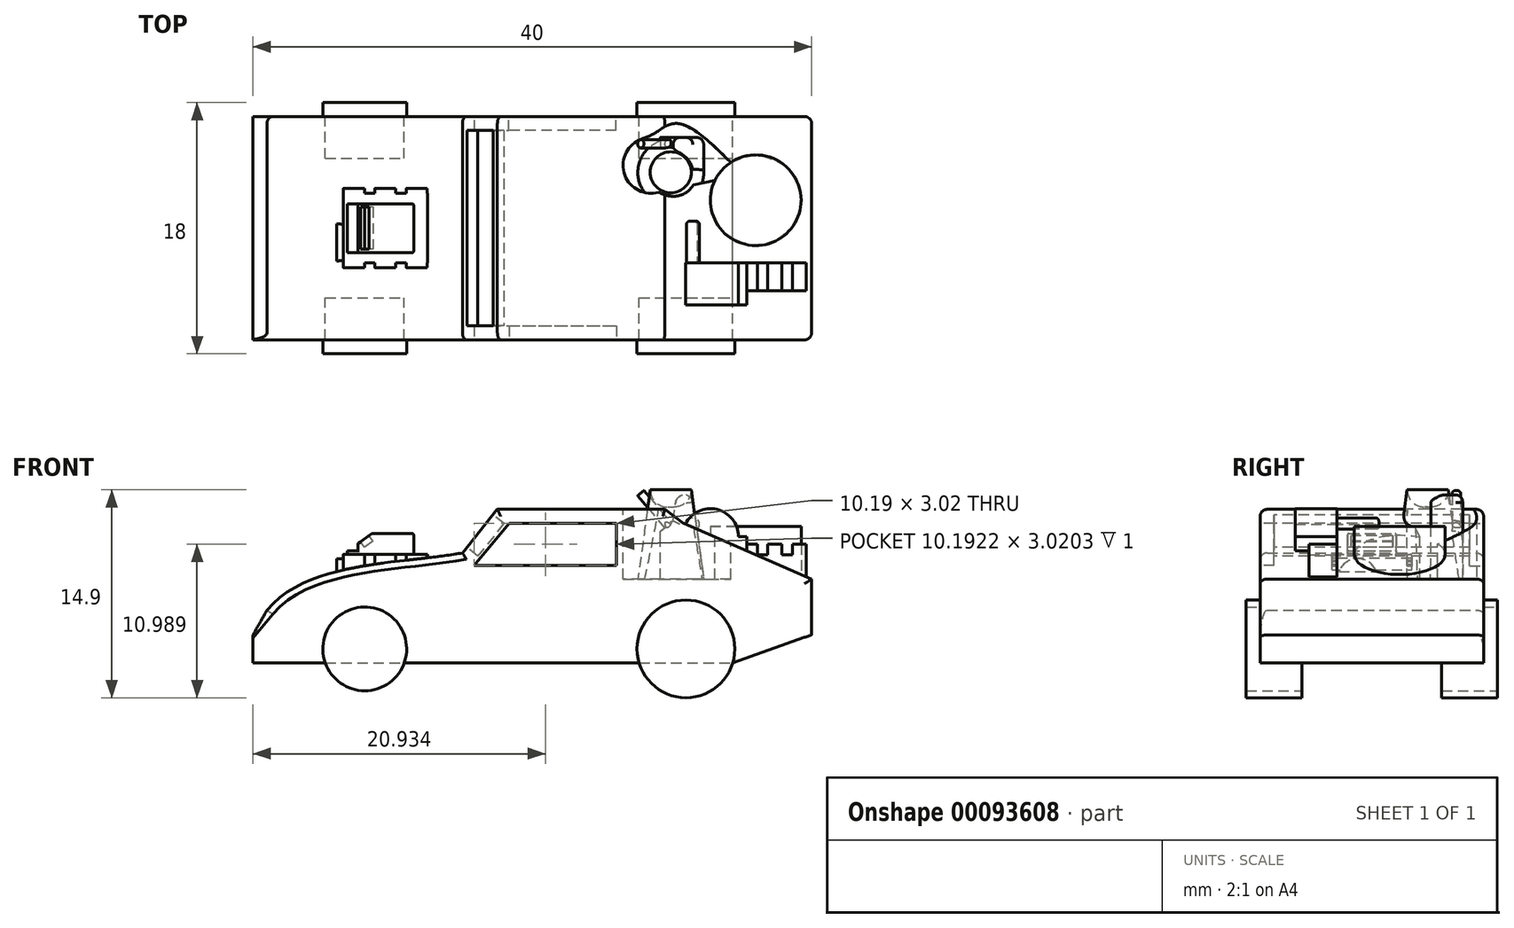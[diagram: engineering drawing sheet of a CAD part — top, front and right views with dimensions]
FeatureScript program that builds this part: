
annotation { "Feature Type Name" : "Feature", "Feature Type Description" : "" }
export const myFeature = defineFeature(function(context is Context, id is Id, definition is map)
    precondition{}
    {
        {
            var Q0;
            Q0=qCreatedBy(makeId("Front.planeOp"),FACE);
            var sketch = newSketch(context, id + "F0", { "sketchPlane" : qUnion([Q0])});
            skLineSegment(sketch, "E0", {"start": v(-19.08, 0) * mm, "end": v(19.92, 0) * mm});
            skLineSegment(sketch, "E1", {"start": v(19.92, 2.22) * mm, "end": v(19.92, -1.78) * mm});
            skLineSegment(sketch, "E2", {"start": v(19.92, -1.78) * mm, "end": v(14.24, -3.78) * mm});
            skLineSegment(sketch, "E3", {"start": v(19.92, 2.22) * mm, "end": v(10.77, 6.21) * mm});
            skLineSegment(sketch, "E4", {"start": v(10.74, 6.23) * mm, "end": v(9.42, 7.22) * mm});
            skLineSegment(sketch, "E5", {"start": v(9.42, 7.22) * mm, "end": v(-2.58, 7.22) * mm});
            skLineSegment(sketch, "E6", {"start": v(-2.58, 7.22) * mm, "end": v(-5.08, 4.1) * mm});
            skFitSpline(sketch, "E7", {"points": [v(-19.08, 0) * mm, v(-5.08, 4.1) * mm], "startDerivative": vector(8.6, 10.5) * mm, "endDerivative": vector(13.58, 2.41) * mm});
            skLineSegment(sketch, "E8", {"start": v(-19.08, 0) * mm, "end": v(-20.08, -1.78) * mm});
            skLineSegment(sketch, "E9", {"start": v(-20.08, -1.78) * mm, "end": v(-20.08, -3.78) * mm});
            skLineSegment(sketch, "E10", {"start": v(-20.08, -3.78) * mm, "end": v(14.24, -3.78) * mm});
            skPoint(sketch, "E11.visualSharp", {"position": v(10.75, 6.22) * mm});
            skArc(sketch, "E11.filletArc", {"start": v(10.74, 6.23) * mm, "mid": v(10.75, 6.22) * mm, "end": v(10.77, 6.21) * mm});
            skSolve(sketch);
        }
        {
            var Q0;
            Q0 = qSketchRegion(id + "F0", true);
            extrude(context, id + "F1", {"entities" : qUnion([Q0]), "endBound" : BoundingType.SYMMETRIC, "depth" : 16 * mm});
        }
        {
            var Q0;
            Q0=makeQuery(id+"F1.opExtrude","CAP_EDGE",EDGE,{"disambiguationData":[OSD([sQuery(id+"F0.wireOp",EDGE,"E7")])],"isStart":false});
            var Q1;
            Q1=makeQuery(id+"F1.opExtrude","CAP_EDGE",EDGE,{"disambiguationData":[OSD([sQuery(id+"F0.wireOp",EDGE,"E6")])],"isStart":false});
            var Q2;
            Q2=makeQuery(id+"F1.opExtrude","CAP_EDGE",EDGE,{"disambiguationData":[OSD([sQuery(id+"F0.wireOp",EDGE,"E5")])],"isStart":false});
            var Q3;
            Q3=makeQuery(id+"F1.opExtrude","CAP_EDGE",EDGE,{"disambiguationData":[OSD([sQuery(id+"F0.wireOp",EDGE,"E3")])],"isStart":false});
            var Q4;
            Q4=makeQuery(id+"F1.opExtrude","CAP_EDGE",EDGE,{"disambiguationData":[OSD([sQuery(id+"F0.wireOp",EDGE,"E4")])],"isStart":false});
            var Q5;
            Q5=makeQuery(id+"F1.opExtrude","CAP_EDGE",EDGE,{"disambiguationData":[OSD([sQuery(id+"F0.wireOp",EDGE,"E8")])],"isStart":true});
            var Q6;
            Q6=makeQuery(id+"F1.opExtrude","CAP_EDGE",EDGE,{"disambiguationData":[OSD([sQuery(id+"F0.wireOp",EDGE,"E7")])],"isStart":true});
            var Q7;
            Q7=makeQuery(id+"F1.opExtrude","CAP_EDGE",EDGE,{"disambiguationData":[OSD([sQuery(id+"F0.wireOp",EDGE,"E6")])],"isStart":true});
            var Q8;
            Q8=makeQuery(id+"F1.opExtrude","CAP_EDGE",EDGE,{"disambiguationData":[OSD([sQuery(id+"F0.wireOp",EDGE,"E5")])],"isStart":true});
            var Q9;
            Q9=makeQuery(id+"F1.opExtrude","CAP_EDGE",EDGE,{"disambiguationData":[OSD([sQuery(id+"F0.wireOp",EDGE,"E4")])],"isStart":true});
            var Q10;
            Q10=makeQuery(id+"F1.opExtrude","CAP_EDGE",EDGE,{"disambiguationData":[OSD([sQuery(id+"F0.wireOp",EDGE,"E3")])],"isStart":true});
            var Q11;
            Q11=makeQuery(id+"F1.opExtrude","CAP_EDGE",EDGE,{"disambiguationData":[OSD([sQuery(id+"F0.wireOp",EDGE,"E1")])],"isStart":false});
            var Q12;
            Q12=makeQuery(id+"F1.opExtrude","CAP_EDGE",EDGE,{"disambiguationData":[OSD([sQuery(id+"F0.wireOp",EDGE,"E1")])],"isStart":true});
            fillet(context, id + "F2", {"entities" : qUnion([Q0, Q1, Q2, Q3, Q4, Q5, Q6, Q7, Q8, Q9, Q10, Q11, Q12]), "radius" : 0.5 * mm, "tangentPropagation" : true, "allowEdgeOverflow" : false});
        }
        {
            var Q0;
            Q0=qCreatedBy(makeId("Top.planeOp"),FACE);
            var sketch = newSketch(context, id + "F3", { "sketchPlane" : qUnion([Q0])});
            skLineSegment(sketch, "E12.bottom", {"start": v(-13.58, 2.5) * mm, "end": v(-7.58, 2.5) * mm});
            skLineSegment(sketch, "E12.top", {"start": v(-13.58, -2.5) * mm, "end": v(-7.58, -2.5) * mm});
            skLineSegment(sketch, "E12.left", {"start": v(-13.58, 2.5) * mm, "end": v(-13.58, -2.5) * mm});
            skLineSegment(sketch, "E12.right", {"start": v(-7.58, 2.5) * mm, "end": v(-7.58, -2.5) * mm});
            skSolve(sketch);
        }
        {
            var Q0;
            Q0 = qSketchRegion(id + "F3", true);
            extrude(context, id + "F4", {"entities" : qUnion([Q0]), "operationType" : NewBodyOperationType.ADD, "depth" : 4 * mm});
        }
        {
            var Q0;
            Q0=qCreatedBy(makeId("Front.planeOp"),FACE);
            var sketch = newSketch(context, id + "F5", { "sketchPlane" : qUnion([Q0])});
            skLineSegment(sketch, "E13", {"start": v(-8.58, 4) * mm, "end": v(-12.58, 4) * mm});
            skLineSegment(sketch, "E14", {"start": v(-12.58, 4.25) * mm, "end": v(-12.58, 4.75) * mm});
            skLineSegment(sketch, "E15", {"start": v(-12.58, 4.75) * mm, "end": v(-11.58, 5.48) * mm});
            skLineSegment(sketch, "E16", {"start": v(-11.58, 5.48) * mm, "end": v(-8.58, 5.48) * mm});
            skLineSegment(sketch, "E17", {"start": v(-8.58, 5.48) * mm, "end": v(-8.58, 4) * mm});
            skLineSegment(sketch, "E18", {"start": v(-12.58, 4) * mm, "end": v(-13.33, 4) * mm});
            skLineSegment(sketch, "E19", {"start": v(-13.33, 4) * mm, "end": v(-13.33, 4.25) * mm});
            skLineSegment(sketch, "E20", {"start": v(-13.33, 4.25) * mm, "end": v(-12.58, 4.25) * mm});
            skSolve(sketch);
        }
        {
            var Q0;
            Q0 = qSketchRegion(id + "F5", true);
            extrude(context, id + "F6", {"entities" : qUnion([Q0]), "operationType" : NewBodyOperationType.ADD, "endBound" : BoundingType.SYMMETRIC, "depth" : 3.5 * mm});
        }
        {
            var Q0;
            Q0=makeQuery(id+"F6.opExtrude","SWEPT_FACE",FACE,{"disambiguationData":[OSD([sQuery(id+"F5.wireOp",EDGE,"E15")])]});
            var sketch = newSketch(context, id + "F7", { "sketchPlane" : qUnion([Q0])});
            skLineSegment(sketch, "E21.bottom", {"start": v(-6.36, 1.5) * mm, "end": v(-7.1, 1.5) * mm});
            skLineSegment(sketch, "E21.top", {"start": v(-6.36, -1.5) * mm, "end": v(-7.1, -1.5) * mm});
            skLineSegment(sketch, "E21.left", {"start": v(-6.36, 1.5) * mm, "end": v(-6.36, -1.5) * mm});
            skLineSegment(sketch, "E21.right", {"start": v(-7.1, 1.5) * mm, "end": v(-7.1, -1.5) * mm});
            skSolve(sketch);
        }
        {
            var Q0;
            Q0 = qSketchRegion(id + "F7", true);
            extrude(context, id + "F8", {"entities" : qUnion([Q0]), "operationType" : NewBodyOperationType.REMOVE, "oppositeDirection" : true, "depth" : 0.5 * mm});
        }
        {
            var Q0;
            Q0=makeQuery(id+"F4.opExtrude","SWEPT_FACE",FACE,{"disambiguationData":[OSD([sQuery(id+"F3.wireOp",EDGE,"E12.left")])]});
            var sketch = newSketch(context, id + "F9", { "sketchPlane" : qUnion([Q0])});
            skCircle(sketch, "E22", {"center": v(1.02, 2.25) * mm, "radius": 1.43 * mm});
            skSolve(sketch);
        }
        {
            var Q0;
            Q0 = qSketchRegion(id + "F9", true);
            extrude(context, id + "F10", {"entities" : qUnion([Q0]), "operationType" : NewBodyOperationType.ADD, "depth" : 0.5 * mm});
        }
        {
            var Q0;
            Q0=qCreatedBy(makeId("Front.planeOp"),FACE);
            var sketch = newSketch(context, id + "F11", { "sketchPlane" : qUnion([Q0])});
            skLineSegment(sketch, "E23", {"start": v(-13.6, 4) * mm, "end": v(-13.6, 2) * mm});
            skLineSegment(sketch, "E24", {"start": v(-13.6, 2) * mm, "end": v(-7.6, 2) * mm});
            skLineSegment(sketch, "E25", {"start": v(-7.6, 2) * mm, "end": v(-7.6, 4) * mm});
            skLineSegment(sketch, "E26", {"start": v(-7.6, 2.66) * mm, "end": v(-7.6, 4) * mm});
            skLineSegment(sketch, "E27", {"start": v(-7.6, 4) * mm, "end": v(-9.1, 4) * mm});
            skLineSegment(sketch, "E28", {"start": v(-9.1, 4) * mm, "end": v(-9.1, 2.66) * mm});
            skLineSegment(sketch, "E29", {"start": v(-9.1, 2.66) * mm, "end": v(-9.86, 2.66) * mm});
            skLineSegment(sketch, "E30", {"start": v(-9.86, 2.66) * mm, "end": v(-9.86, 4) * mm});
            skLineSegment(sketch, "E31", {"start": v(-9.86, 4) * mm, "end": v(-11.36, 4) * mm});
            skLineSegment(sketch, "E32", {"start": v(-11.36, 4) * mm, "end": v(-11.36, 2.45) * mm});
            skLineSegment(sketch, "E33", {"start": v(-11.36, 2.45) * mm, "end": v(-12.1, 2.45) * mm});
            skLineSegment(sketch, "E34", {"start": v(-12.1, 2.45) * mm, "end": v(-12.1, 4) * mm});
            skLineSegment(sketch, "E35", {"start": v(-12.1, 4) * mm, "end": v(-13.6, 4) * mm});
            skSolve(sketch);
        }
        {
            var Q0;
            Q0 = qSketchRegion(id + "F11", true);
            extrude(context, id + "F12", {"entities" : qUnion([Q0]), "operationType" : NewBodyOperationType.ADD, "endBound" : BoundingType.SYMMETRIC, "depth" : 5.7 * mm});
        }
        {
            var Q0;
            Q0=makeQuery(id+"F12.opExtrude","CAP_EDGE",EDGE,{"disambiguationData":[OSD([sQuery(id+"F11.wireOp",EDGE,"E35")])],"isStart":false});
            var Q1;
            Q1=makeQuery(id+"F12.opExtrude","CAP_EDGE",EDGE,{"disambiguationData":[OSD([sQuery(id+"F11.wireOp",EDGE,"E31")])],"isStart":false});
            var Q2;
            Q2=makeQuery(id+"F12.opExtrude","CAP_EDGE",EDGE,{"disambiguationData":[OSD([sQuery(id+"F11.wireOp",EDGE,"E27")])],"isStart":false});
            var Q3;
            Q3=makeQuery(id+"F12.opExtrude","CAP_EDGE",EDGE,{"disambiguationData":[OSD([sQuery(id+"F11.wireOp",EDGE,"E31")])],"isStart":true});
            var Q4;
            Q4=makeQuery(id+"F12.opExtrude","CAP_EDGE",EDGE,{"disambiguationData":[OSD([sQuery(id+"F11.wireOp",EDGE,"E35")])],"isStart":true});
            var Q5;
            Q5=makeQuery(id+"F12.opExtrude","CAP_EDGE",EDGE,{"disambiguationData":[OSD([sQuery(id+"F11.wireOp",EDGE,"E27")])],"isStart":true});
            var Q6;
            Q6=makeQuery(id+"F6.opExtrude","CAP_EDGE",EDGE,{"disambiguationData":[OSD([sQuery(id+"F5.wireOp",EDGE,"E15")])],"isStart":true});
            var Q7;
            Q7=makeQuery(id+"F6.opExtrude","CAP_EDGE",EDGE,{"disambiguationData":[OSD([sQuery(id+"F5.wireOp",EDGE,"E16")])],"isStart":true});
            var Q8;
            Q8=makeQuery(id+"F6.opExtrude","SWEPT_EDGE",EDGE,{"disambiguationData":[OSD([sQuery(id+"F5.wireOp",EDGE,"E16"),sQuery(id+"F5.wireOp",EDGE,"E17")])]});
            var Q9;
            Q9=makeQuery(id+"F6.opExtrude","CAP_EDGE",EDGE,{"disambiguationData":[OSD([sQuery(id+"F5.wireOp",EDGE,"E16")])],"isStart":false});
            var Q10;
            Q10=makeQuery(id+"F6.opExtrude","CAP_EDGE",EDGE,{"disambiguationData":[OSD([sQuery(id+"F5.wireOp",EDGE,"E15")])],"isStart":false});
            var Q11;
            Q11=makeQuery(id+"F6.opExtrude","SWEPT_EDGE",EDGE,{"disambiguationData":[OSD([sQuery(id+"F5.wireOp",EDGE,"E15"),sQuery(id+"F5.wireOp",EDGE,"E16")])]});
            var Q12;
            Q12=makeQuery(id+"F6.opExtrude","SWEPT_EDGE",EDGE,{"disambiguationData":[OSD([sQuery(id+"F5.wireOp",EDGE,"E14"),sQuery(id+"F5.wireOp",EDGE,"E15")])]});
            var Q13;
            Q13=makeQuery(id+"F6.opExtrude","CAP_EDGE",EDGE,{"disambiguationData":[OSD([sQuery(id+"F5.wireOp",EDGE,"E14")])],"isStart":false});
            var Q14;
            Q14=makeQuery(id+"F6.opExtrude","CAP_EDGE",EDGE,{"disambiguationData":[OSD([sQuery(id+"F5.wireOp",EDGE,"E14")])],"isStart":true});
            var Q15;
            Q15=makeQuery(id+"F6.opExtrude","CAP_EDGE",EDGE,{"disambiguationData":[OSD([sQuery(id+"F5.wireOp",EDGE,"E17")])],"isStart":false});
            var Q16;
            Q16=makeQuery(id+"F6.opExtrude","CAP_EDGE",EDGE,{"disambiguationData":[OSD([sQuery(id+"F5.wireOp",EDGE,"E17")])],"isStart":true});
            fillet(context, id + "F13", {"entities" : qUnion([Q0, Q1, Q2, Q3, Q4, Q5, Q6, Q7, Q8, Q9, Q10, Q11, Q12, Q13, Q14, Q15, Q16]), "radius" : 0.1 * mm, "tangentPropagation" : true, "allowEdgeOverflow" : false});
        }
        {
            var Q0;
            Q0=qCreatedBy(makeId("Front.planeOp"),FACE);
            cPlane(context, id + "F14", {"entities" : qUnion([Q0]), "cplaneType" : CPlaneType.OFFSET, "offset" : 2.5 * mm, "width" : 150 * mm, "height" : 150 * mm});
        }
        {
            var Q0;
            Q0=qCreatedBy(id+"F14.planeOp",FACE);
            var sketch = newSketch(context, id + "F15", { "sketchPlane" : qUnion([Q0])});
            skArc(sketch, "E36", {"start": v(14.68, 5.27) * mm, "mid": v(11.82, 7.08) * mm, "end": v(11.42, 3.72) * mm});
            skLineSegment(sketch, "E37", {"start": v(12.68, 5.27) * mm, "end": v(15.28, 5.27) * mm});
            skLineSegment(sketch, "E38", {"start": v(15.28, 5.27) * mm, "end": v(15.28, 3.72) * mm});
            skLineSegment(sketch, "E39", {"start": v(15.28, 3.72) * mm, "end": v(11.42, 3.72) * mm});
            skSolve(sketch);
        }
        {
            var Q0;
            Q0 = qSketchRegion(id + "F15", true);
            extrude(context, id + "F16", {"entities" : qUnion([Q0]), "operationType" : NewBodyOperationType.ADD, "depth" : 3 * mm});
        }
        {
            var Q0;
            Q0=qCreatedBy(id+"F14.planeOp",FACE);
            var sketch = newSketch(context, id + "F17", { "sketchPlane" : qUnion([Q0])});
            skLineSegment(sketch, "E40", {"start": v(14.73, 4.72) * mm, "end": v(16.03, 4.72) * mm});
            skLineSegment(sketch, "E41", {"start": v(16.03, 4.72) * mm, "end": v(16.03, 3.96) * mm});
            skLineSegment(sketch, "E42", {"start": v(16.78, 3.96) * mm, "end": v(16.78, 4.72) * mm});
            skLineSegment(sketch, "E43", {"start": v(16.78, 4.72) * mm, "end": v(17.78, 4.72) * mm});
            skLineSegment(sketch, "E44", {"start": v(17.78, 4.72) * mm, "end": v(17.78, 3.96) * mm});
            skLineSegment(sketch, "E45", {"start": v(18.53, 3.96) * mm, "end": v(18.53, 4.72) * mm});
            skLineSegment(sketch, "E46", {"start": v(16.03, 3.96) * mm, "end": v(16.78, 3.96) * mm});
            skLineSegment(sketch, "E47", {"start": v(17.78, 3.96) * mm, "end": v(18.53, 3.96) * mm});
            skLineSegment(sketch, "E48", {"start": v(18.53, 4.72) * mm, "end": v(19.53, 4.72) * mm});
            skLineSegment(sketch, "E49", {"start": v(19.53, 4.72) * mm, "end": v(19.53, 1.8) * mm});
            skLineSegment(sketch, "E50", {"start": v(19.53, 1.8) * mm, "end": v(14.73, 1.8) * mm});
            skLineSegment(sketch, "E51", {"start": v(14.73, 1.8) * mm, "end": v(14.73, 4.72) * mm});
            skPoint(sketch, "E52.orphan", {"position": v(15.29, 4.72) * mm});
            skPoint(sketch, "E53.start.orphan", {"position": v(16.03, 3.2) * mm});
            skPoint(sketch, "E54.orphan", {"position": v(16.78, 3.2) * mm});
            skSolve(sketch);
        }
        {
            var Q0;
            Q0 = qSketchRegion(id + "F17", true);
            extrude(context, id + "F18", {"entities" : qUnion([Q0]), "operationType" : NewBodyOperationType.ADD, "depth" : 2 * mm});
        }
        {
            var Q0;
            Q0=qCreatedBy(makeId("Top.planeOp"),FACE);
            var sketch = newSketch(context, id + "F19", { "sketchPlane" : qUnion([Q0])});
            skCircle(sketch, "E55", {"center": v(15.92, 2) * mm, "radius": 3.25 * mm});
            skSolve(sketch);
        }
        {
            var Q0;
            Q0 = qSketchRegion(id + "F19", true);
            extrude(context, id + "F20", {"entities" : qUnion([Q0]), "operationType" : NewBodyOperationType.ADD, "depth" : 6 * mm});
        }
        {
            var Q0;
            Q0=makeQuery(id+"F18.boolean.opBoolean","MERGE",FACE,{"derivedFrom":[makeQuery(id+"F16.opExtrude","CAP_FACE",FACE,{"disambiguationData":[OSD([sQuery(id+"F15.wireOp",EDGE,"E36"),sQuery(id+"F15.wireOp",EDGE,"E37"),sQuery(id+"F15.wireOp",EDGE,"E38"),sQuery(id+"F15.wireOp",EDGE,"E39")])],"isStart":true}),makeQuery(id+"F18.opExtrude","CAP_FACE",FACE,{"disambiguationData":[OSD([sQuery(id+"F17.wireOp",EDGE,"E40"),sQuery(id+"F17.wireOp",EDGE,"E41"),sQuery(id+"F17.wireOp",EDGE,"E42"),sQuery(id+"F17.wireOp",EDGE,"E43"),sQuery(id+"F17.wireOp",EDGE,"E44"),sQuery(id+"F17.wireOp",EDGE,"E45"),sQuery(id+"F17.wireOp",EDGE,"E46"),sQuery(id+"F17.wireOp",EDGE,"E47"),sQuery(id+"F17.wireOp",EDGE,"E48"),sQuery(id+"F17.wireOp",EDGE,"E49"),sQuery(id+"F17.wireOp",EDGE,"E50"),sQuery(id+"F17.wireOp",EDGE,"E51")])],"isStart":true})]});
            var sketch = newSketch(context, id + "F21", { "sketchPlane" : qUnion([Q0])});
            skCircle(sketch, "E56", {"center": v(-11.42, 6.15) * mm, "radius": 0.47 * mm});
            skSolve(sketch);
        }
        {
            var Q0;
            Q0 = qSketchRegion(id + "F21", true);
            extrude(context, id + "F22", {"entities" : qUnion([Q0]), "operationType" : NewBodyOperationType.ADD, "depth" : 3 * mm});
        }
        {
            var Q0;
            Q0=makeQuery(id+"F22.opExtrude","CAP_EDGE",EDGE,{"disambiguationData":[OSD([sQuery(id+"F21.wireOp",EDGE,"E56")])],"isStart":false});
            fillet(context, id + "F23", {"entities" : qUnion([Q0]), "radius" : 0.25 * mm, "tangentPropagation" : true, "allowEdgeOverflow" : false});
        }
        {
            var Q0;
            Q0=makeQuery(id+"F1.opExtrude","SWEPT_FACE",FACE,{"disambiguationData":[OSD([sQuery(id+"F0.wireOp",EDGE,"E5")])]});
            var sketch = newSketch(context, id + "F24", { "sketchPlane" : qUnion([Q0])});
            skArc(sketch, "E57", {"start": v(7.77, 6.4) * mm, "mid": v(6.55, 3.78) * mm, "end": v(9.21, 2.67) * mm});
            skFitSpline(sketch, "E58", {"points": [v(8.39, 6.5) * mm, v(10.32, 7.5) * mm, v(14.03, 4.82) * mm], "startDerivative": vector(4.42, 3.87) * mm, "endDerivative": vector(6.71, -6.6) * mm});
            skLineSegment(sketch, "E59", {"start": v(9.21, 2.67) * mm, "end": v(13, 3.43) * mm});
            skArc(sketch, "E60", {"start": v(14.13, 4.72) * mm, "mid": v(13.48, 4.15) * mm, "end": v(13, 3.43) * mm});
            skLineSegment(sketch, "E61", {"start": v(14.03, 4.82) * mm, "end": v(14.13, 4.72) * mm});
            skArc(sketch, "E62.filletArc", {"start": v(7.77, 6.4) * mm, "mid": v(8.45, 6.68) * mm, "end": v(9.08, 7.06) * mm});
            skSolve(sketch);
        }
        {
            var Q0;
            Q0 = qSketchRegion(id + "F24", true);
            extrude(context, id + "F25", {"entities" : qUnion([Q0]), "operationType" : NewBodyOperationType.REMOVE, "oppositeDirection" : true, "depth" : 5 * mm});
        }
        {
            var Q0;
            Q0=makeQuery(id+"F1.opExtrude","CAP_FACE",FACE,{"disambiguationData":[OSD([sQuery(id+"F0.wireOp",EDGE,"E1"),sQuery(id+"F0.wireOp",EDGE,"E2"),sQuery(id+"F0.wireOp",EDGE,"E3"),sQuery(id+"F0.wireOp",EDGE,"E4"),sQuery(id+"F0.wireOp",EDGE,"E5"),sQuery(id+"F0.wireOp",EDGE,"E6"),sQuery(id+"F0.wireOp",EDGE,"E7"),sQuery(id+"F0.wireOp",EDGE,"E8"),sQuery(id+"F0.wireOp",EDGE,"E9"),sQuery(id+"F0.wireOp",EDGE,"E10"),sQuery(id+"F0.wireOp",EDGE,"E11.filletArc")])],"isStart":true});
            cPlane(context, id + "F26", {"entities" : qUnion([Q0]), "cplaneType" : CPlaneType.OFFSET, "offset" : 4 * mm, "oppositeDirection" : true, "width" : 150 * mm, "height" : 150 * mm});
        }
        {
            var Q0;
            Q0=qCreatedBy(id+"F26.planeOp",FACE);
            var sketch = newSketch(context, id + "F27", { "sketchPlane" : qUnion([Q0])});
            skLineSegment(sketch, "E63", {"start": v(-9.84, 1.22) * mm, "end": v(-9.84, 9.86) * mm});
            skArc(sketch, "E64", {"start": v(-8.36, 8.62) * mm, "mid": v(-8.8, 9.58) * mm, "end": v(-9.84, 9.86) * mm});
            skLineSegment(sketch, "E65", {"start": v(-8.36, 8.62) * mm, "end": v(-7.34, 1.22) * mm});
            skLineSegment(sketch, "E66", {"start": v(-7.34, 1.22) * mm, "end": v(-9.84, 1.22) * mm});
            skLineSegment(sketch, "E67", {"start": v(-9.84, 9.86) * mm, "end": v(-9.84, 11.33) * mm});
            skSolve(sketch);
        }
        {
            var Q0;
            Q0 = qSketchRegion(id + "F27", true);
            var Q1;
            Q1=sQuery(id+"F27.wireOp",EDGE,"E67");
            revolve(context, id + "F28", {"operationType" : NewBodyOperationType.ADD, "entities" : qUnion([Q0]), "axis" : qUnion([Q1]), "revolveType" : RevolveType.FULL});
        }
        {
            var Q0;
            Q0=qCreatedBy(id+"F26.planeOp",FACE);
            var sketch = newSketch(context, id + "F29", { "sketchPlane" : qUnion([Q0])});
            skLineSegment(sketch, "E68", {"start": v(-11.41, 7.72) * mm, "end": v(-12.48, 0.2) * mm});
            skLineSegment(sketch, "E69", {"start": v(-12.48, 0.2) * mm, "end": v(-9.09, 0.2) * mm});
            skLineSegment(sketch, "E70", {"start": v(-9.09, 0.2) * mm, "end": v(-9.09, 5.64) * mm});
            skLineSegment(sketch, "E71", {"start": v(-9.09, 5.64) * mm, "end": v(-10, 6.41) * mm});
            skLineSegment(sketch, "E72", {"start": v(-10, 6.41) * mm, "end": v(-10.19, 7.72) * mm});
            skArc(sketch, "E73", {"start": v(-10.19, 7.72) * mm, "mid": v(-10.8, 8.25) * mm, "end": v(-11.41, 7.72) * mm});
            skPoint(sketch, "E74.orphan", {"position": v(-9.09, 7.72) * mm});
            skSolve(sketch);
        }
        {
            var Q0;
            Q0 = qSketchRegion(id + "F29", true);
            extrude(context, id + "F30", {"entities" : qUnion([Q0]), "operationType" : NewBodyOperationType.ADD, "depth" : 2.5 * mm});
        }
        {
            var Q0;
            Q0=makeQuery(id+"F30.opExtrude","SWEPT_FACE",FACE,{"disambiguationData":[OSD([sQuery(id+"F29.wireOp",EDGE,"E71")])]});
            var sketch = newSketch(context, id + "F31", { "sketchPlane" : qUnion([Q0])});
            skCircle(sketch, "E75", {"center": v(11.28, 6.05) * mm, "radius": 0.3 * mm});
            skSolve(sketch);
        }
        {
            var Q0;
            Q0 = qSketchRegion(id + "F31", true);
            extrude(context, id + "F32", {"entities" : qUnion([Q0]), "operationType" : NewBodyOperationType.ADD, "depth" : 3 * mm});
        }
        {
            var Q0;
            Q0=makeQuery(id+"F30.opExtrude","CAP_EDGE",EDGE,{"disambiguationData":[OSD([sQuery(id+"F29.wireOp",EDGE,"E68")])],"isStart":false});
            var Q1;
            Q1=makeQuery(id+"F30.opExtrude","CAP_EDGE",EDGE,{"disambiguationData":[OSD([sQuery(id+"F29.wireOp",EDGE,"E73")])],"isStart":false});
            var Q2;
            Q2=makeQuery(id+"F30.opExtrude","CAP_EDGE",EDGE,{"disambiguationData":[OSD([sQuery(id+"F29.wireOp",EDGE,"E72")])],"isStart":false});
            var Q3;
            Q3=makeQuery(id+"F30.opExtrude","CAP_EDGE",EDGE,{"disambiguationData":[OSD([sQuery(id+"F29.wireOp",EDGE,"E71")])],"isStart":false});
            fillet(context, id + "F33", {"entities" : qUnion([Q0, Q1, Q2, Q3]), "radius" : 0.5 * mm, "tangentPropagation" : true, "allowEdgeOverflow" : false});
        }
        {
            var Q0;
            Q0=makeQuery(id+"F1.opExtrude","SWEPT_FACE",FACE,{"disambiguationData":[OSD([sQuery(id+"F0.wireOp",EDGE,"E6")])]});
            var sketch = newSketch(context, id + "F34", { "sketchPlane" : qUnion([Q0])});
            skLineSegment(sketch, "E76.bottom", {"start": v(-7, 3.52) * mm, "end": v(7, 3.52) * mm});
            skLineSegment(sketch, "E76.top", {"start": v(-7, 0.52) * mm, "end": v(7, 0.52) * mm});
            skLineSegment(sketch, "E76.left", {"start": v(-7, 3.52) * mm, "end": v(-7, 0.52) * mm});
            skLineSegment(sketch, "E76.right", {"start": v(7, 3.52) * mm, "end": v(7, 0.52) * mm});
            skSolve(sketch);
        }
        {
            var Q0;
            Q0 = qSketchRegion(id + "F34", true);
            extrude(context, id + "F35", {"entities" : qUnion([Q0]), "operationType" : NewBodyOperationType.REMOVE, "oppositeDirection" : true, "depth" : 1 * mm});
        }
        {
            var Q0;
            Q0=makeQuery(id+"F1.opExtrude","CAP_FACE",FACE,{"disambiguationData":[OSD([sQuery(id+"F0.wireOp",EDGE,"E1"),sQuery(id+"F0.wireOp",EDGE,"E2"),sQuery(id+"F0.wireOp",EDGE,"E3"),sQuery(id+"F0.wireOp",EDGE,"E4"),sQuery(id+"F0.wireOp",EDGE,"E5"),sQuery(id+"F0.wireOp",EDGE,"E6"),sQuery(id+"F0.wireOp",EDGE,"E7"),sQuery(id+"F0.wireOp",EDGE,"E8"),sQuery(id+"F0.wireOp",EDGE,"E9"),sQuery(id+"F0.wireOp",EDGE,"E10"),sQuery(id+"F0.wireOp",EDGE,"E11.filletArc")])],"isStart":true});
            var sketch = newSketch(context, id + "F36", { "sketchPlane" : qUnion([Q0])});
            skLineSegment(sketch, "E77.0", {"start": v(4.22, 3.17) * mm, "end": v(1.76, 6.25) * mm});
            skLineSegment(sketch, "E78.0", {"start": v(-10.92, 11.72) * mm, "end": v(-13.03, 10.13) * mm});
            skLineSegment(sketch, "E78.1", {"start": v(4.74, 11.72) * mm, "end": v(-10.92, 11.72) * mm});
            skLineSegment(sketch, "E78.2", {"start": v(-13.03, 10.13) * mm, "end": v(-24.42, 5.17) * mm});
            skLineSegment(sketch, "E78.3", {"start": v(7.49, 8.3) * mm, "end": v(4.74, 11.72) * mm});
            skFitSpline(sketch, "E78.4", {"points": [v(22.51, 2.91) * mm, v(22.32, 3.15) * mm, v(21.92, 3.58) * mm, v(21.3, 4.17) * mm, v(20.65, 4.69) * mm, v(20, 5.13) * mm, v(19.36, 5.52) * mm, v(18.5, 5.97) * mm, v(17.45, 6.43) * mm, v(16.25, 6.84) * mm, v(14.72, 7.26) * mm, v(13.27, 7.54) * mm, v(11.9, 7.76) * mm, v(10.9, 7.9) * mm, v(9.94, 8) * mm, v(9.01, 8.11) * mm, v(8.26, 8.2) * mm, v(7.69, 8.27) * mm, v(7.26, 8.32) * mm, v(6.85, 8.37) * mm, v(6.47, 8.43) * mm, v(6.1, 8.49) * mm, v(5.82, 8.54) * mm, v(5.68, 8.56) * mm]});
            skLineSegment(sketch, "E78.5", {"start": v(25.08, -1.5) * mm, "end": v(22.8, 2.56) * mm});
            skLineSegment(sketch, "E78.6", {"start": v(-24.42, 5.17) * mm, "end": v(-24.42, -5.5) * mm});
            skLineSegment(sketch, "E78.7", {"start": v(-24.42, -5.5) * mm, "end": v(-15.1, -8.78) * mm});
            skLineSegment(sketch, "E78.8", {"start": v(-15.1, -8.78) * mm, "end": v(25.08, -8.78) * mm});
            skLineSegment(sketch, "E78.9", {"start": v(25.08, -8.78) * mm, "end": v(25.08, -1.5) * mm});
            skLineSegment(sketch, "E79.0", {"start": v(-5.92, 6.22) * mm, "end": v(1.78, 6.22) * mm});
            skFitSpline(sketch, "E80.4", {"points": [v(22.51, 2.91) * mm, v(22.32, 3.15) * mm, v(21.92, 3.58) * mm, v(21.3, 4.17) * mm, v(20.65, 4.69) * mm, v(20, 5.13) * mm, v(19.36, 5.52) * mm, v(18.5, 5.97) * mm, v(17.45, 6.43) * mm, v(16.25, 6.84) * mm, v(14.72, 7.26) * mm, v(13.27, 7.54) * mm, v(11.9, 7.76) * mm, v(10.9, 7.9) * mm, v(9.94, 8) * mm, v(9.01, 8.11) * mm, v(8.26, 8.2) * mm, v(7.69, 8.27) * mm, v(7.26, 8.32) * mm, v(6.85, 8.37) * mm, v(6.47, 8.43) * mm, v(6.1, 8.49) * mm, v(5.82, 8.54) * mm, v(5.68, 8.56) * mm]});
            skLineSegment(sketch, "E81", {"start": v(-5.92, 6.22) * mm, "end": v(-5.92, 3.17) * mm});
            skLineSegment(sketch, "E82", {"start": v(-5.92, 3.17) * mm, "end": v(4.22, 3.17) * mm});
            skSolve(sketch);
        }
        {
            var Q0;
            Q0 = qSketchRegion(id + "F36", true);
            extrude(context, id + "F37", {"entities" : qUnion([Q0]), "operationType" : NewBodyOperationType.REMOVE, "oppositeDirection" : true, "depth" : 1 * mm});
        }
        {
            var Q0;
            Q0=makeQuery(id+"F1.opExtrude","CAP_FACE",FACE,{"disambiguationData":[OSD([sQuery(id+"F0.wireOp",EDGE,"E1"),sQuery(id+"F0.wireOp",EDGE,"E2"),sQuery(id+"F0.wireOp",EDGE,"E3"),sQuery(id+"F0.wireOp",EDGE,"E4"),sQuery(id+"F0.wireOp",EDGE,"E5"),sQuery(id+"F0.wireOp",EDGE,"E6"),sQuery(id+"F0.wireOp",EDGE,"E7"),sQuery(id+"F0.wireOp",EDGE,"E8"),sQuery(id+"F0.wireOp",EDGE,"E9"),sQuery(id+"F0.wireOp",EDGE,"E10"),sQuery(id+"F0.wireOp",EDGE,"E11.filletArc")])],"isStart":false});
            var sketch = newSketch(context, id + "F38", { "sketchPlane" : qUnion([Q0])});
            skLineSegment(sketch, "E83.0", {"start": v(-1.74, 6.22) * mm, "end": v(5.95, 6.22) * mm});
            skLineSegment(sketch, "E84", {"start": v(-4.24, 3.2) * mm, "end": v(-1.74, 6.22) * mm});
            skLineSegment(sketch, "E85", {"start": v(-4.24, 3.2) * mm, "end": v(5.95, 3.2) * mm});
            skLineSegment(sketch, "E86", {"start": v(5.95, 3.2) * mm, "end": v(5.95, 6.22) * mm});
            skLineSegment(sketch, "E87", {"start": v(5.95, 6.22) * mm, "end": v(-1.74, 6.22) * mm});
            skSolve(sketch);
        }
        {
            var Q0;
            Q0 = qSketchRegion(id + "F38", true);
            extrude(context, id + "F39", {"entities" : qUnion([Q0]), "operationType" : NewBodyOperationType.REMOVE, "oppositeDirection" : true, "depth" : 1 * mm});
        }
        {
            var Q0;
            Q0=qCreatedBy(makeId("Front.planeOp"),FACE);
            var sketch = newSketch(context, id + "F40", { "sketchPlane" : qUnion([Q0])});
            skCircle(sketch, "E88", {"center": v(10.92, -2.78) * mm, "radius": 3.5 * mm});
            skCircle(sketch, "E89", {"center": v(-12.08, -2.78) * mm, "radius": 3 * mm});
            skSolve(sketch);
        }
        {
            var Q0;
            Q0 = qSketchRegion(id + "F40", true);
            extrude(context, id + "F41", {"entities" : qUnion([Q0]), "operationType" : NewBodyOperationType.ADD, "endBound" : BoundingType.SYMMETRIC, "depth" : 18 * mm});
        }
        {
            var Q0;
            Q0=qCreatedBy(makeId("Front.planeOp"),FACE);
            var sketch = newSketch(context, id + "F42", { "sketchPlane" : qUnion([Q0])});
            skLineSegment(sketch, "E90", {"start": v(20.9, -3.78) * mm, "end": v(20.9, -7.19) * mm});
            skLineSegment(sketch, "E91", {"start": v(20.9, -7.19) * mm, "end": v(-20.2, -7.19) * mm});
            skLineSegment(sketch, "E92", {"start": v(-20.2, -7.19) * mm, "end": v(-20.2, -3.78) * mm});
            skLineSegment(sketch, "E93", {"start": v(-20.2, -3.78) * mm, "end": v(20.9, -3.78) * mm});
            skSolve(sketch);
        }
        {
            var Q0;
            Q0 = qSketchRegion(id + "F42", true);
            extrude(context, id + "F43", {"entities" : qUnion([Q0]), "operationType" : NewBodyOperationType.REMOVE, "endBound" : BoundingType.SYMMETRIC, "oppositeDirection" : true, "depth" : 10 * mm});
        }
    });
